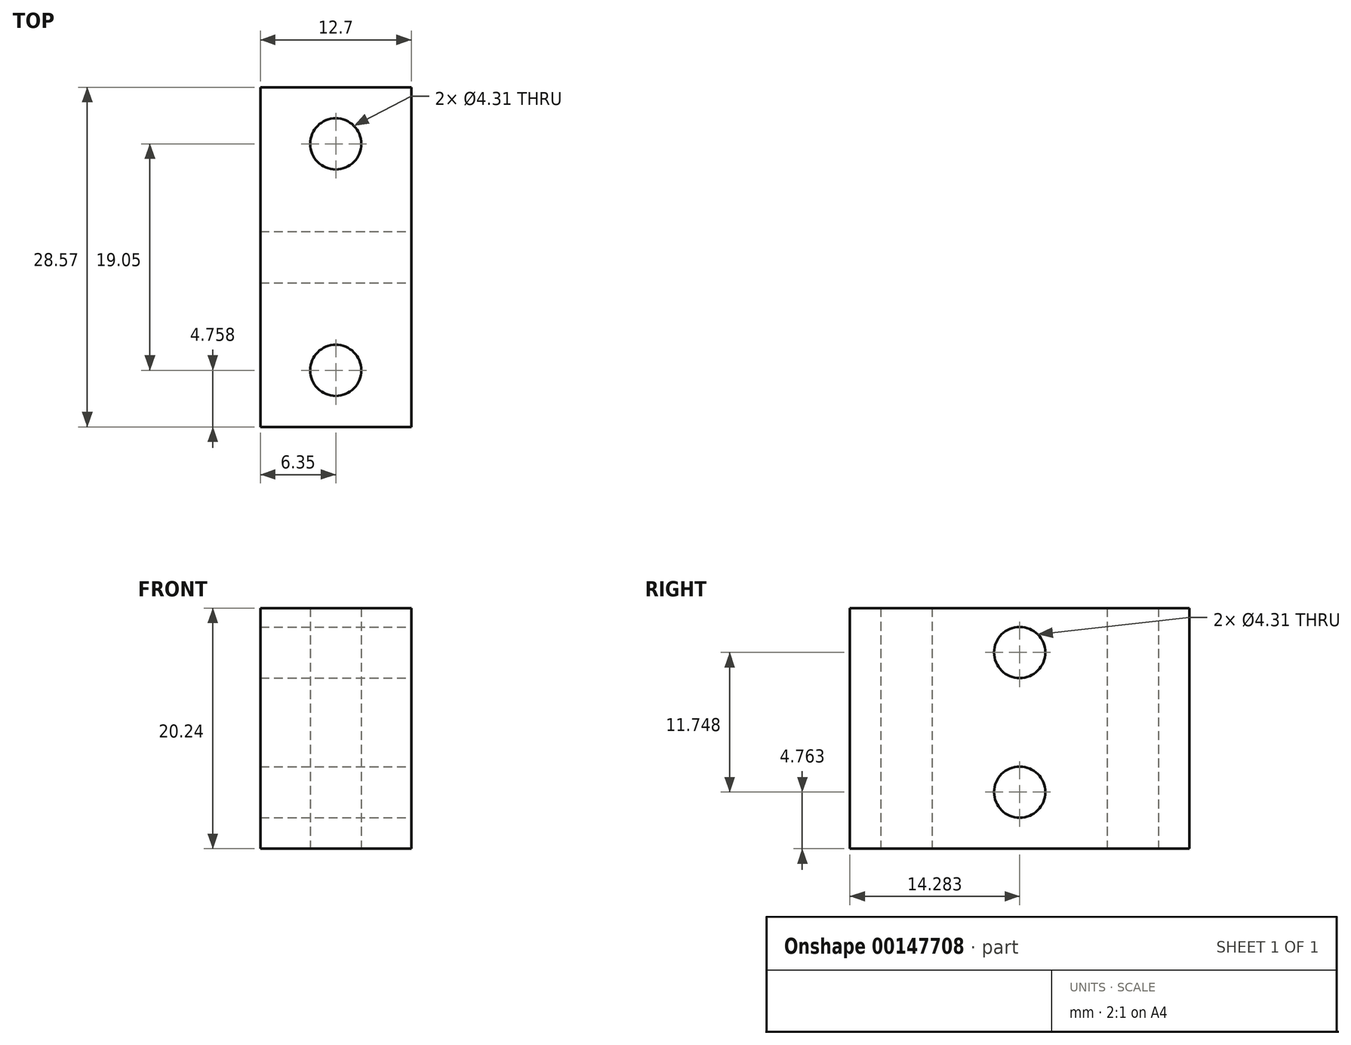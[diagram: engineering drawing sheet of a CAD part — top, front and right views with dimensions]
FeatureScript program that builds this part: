
annotation { "Feature Type Name" : "Feature", "Feature Type Description" : "" }
export const myFeature = defineFeature(function(context is Context, id is Id, definition is map)
    precondition{}
    {
        {
            var Q0;
            Q0=qCreatedBy(makeId("Top.planeOp"),FACE);
            var sketch = newSketch(context, id + "F0", { "sketchPlane" : qUnion([Q0])});
            skLineSegment(sketch, "E0.bottom", {"start": v(0, 0) * mm, "end": v(12.7, 0) * mm});
            skLineSegment(sketch, "E0.top", {"start": v(0, -28.57) * mm, "end": v(12.7, -28.57) * mm});
            skLineSegment(sketch, "E0.left", {"start": v(0, 0) * mm, "end": v(0, -28.58) * mm});
            skLineSegment(sketch, "E0.right", {"start": v(12.7, 0) * mm, "end": v(12.7, -28.57) * mm});
            skLineSegment(sketch, "E1", {"start": v(6.35, 0) * mm, "end": v(6.35, -4.76) * mm, "construction": true});
            skLineSegment(sketch, "E2", {"start": v(6.35, -4.76) * mm, "end": v(6.35, -23.81) * mm, "construction": true});
            skCircle(sketch, "E3", {"center": v(6.35, -4.76) * mm, "radius": 2.15 * mm});
            skCircle(sketch, "E4", {"center": v(6.35, -23.81) * mm, "radius": 2.15 * mm});
            skLineSegment(sketch, "E5", {"start": v(6.35, -23.81) * mm, "end": v(6.35, -28.57) * mm, "construction": true});
            skSolve(sketch);
        }
        {
            var Q0;
            Q0=qSketchRegion(id+"F0",true);
            extrude(context, id + "F1", {"entities" : qUnion([Q0]), "depth" : 20.24 * mm});
        }
        {
            var Q0;
            Q0=makeQuery(id+"F1.opExtrude","SWEPT_FACE",FACE,{"disambiguationData":[OSD([sQuery(id+"F0.wireOp",EDGE,"E0.right")])]});
            var sketch = newSketch(context, id + "F2", { "sketchPlane" : qUnion([Q0])});
            skCircle(sketch, "E6", {"center": v(-14.29, 4.76) * mm, "radius": 2.15 * mm});
            skLineSegment(sketch, "E7", {"start": v(-14.29, 4.76) * mm, "end": v(-14.29, 0) * mm, "construction": true});
            skLineSegment(sketch, "E8", {"start": v(-14.29, 4.76) * mm, "end": v(-14.29, 16.51) * mm, "construction": true});
            skCircle(sketch, "E9", {"center": v(-14.29, 16.51) * mm, "radius": 2.15 * mm});
            skSolve(sketch);
        }
        {
            var Q0;
            Q0=qSketchRegion(id+"F2",true);
            var Q1;
            Q1=makeQuery(id+"F1.opExtrude","SWEPT_FACE",FACE,{"disambiguationData":[OSD([sQuery(id+"F0.wireOp",EDGE,"E0.left")])]});
            extrude(context, id + "F3", {"entities" : qUnion([Q0]), "operationType" : NewBodyOperationType.REMOVE, "endBound" : BoundingType.UP_TO_SURFACE, "oppositeDirection" : true, "endBoundEntityFace" : qUnion([Q1]), "depth" : 25.4 * mm});
        }
    });
